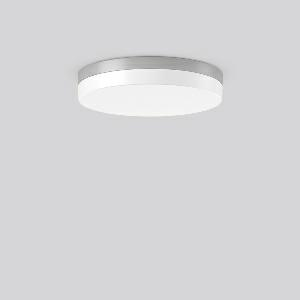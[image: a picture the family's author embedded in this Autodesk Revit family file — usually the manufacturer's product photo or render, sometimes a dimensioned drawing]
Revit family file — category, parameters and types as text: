
# Revit family: flat_slim_round_312632_004_c585
name_source: partatom
category: Lighting Fixtures
units: mm (PartAtom-declared; Revit-internal decimal feet)

## family parameters
Cut with Voids When Loaded = No
Host = Face
Light Source = No
Part Type = Normal
Room Calculation Point = No
Round Connector Dimension = Use Diameter
Shared = No

## types (1)
- MultiLumen 1 830 (1 x LED Modul 830, 2400 lm, 3000)
    Apparent Load = 20 VA
    CIE Flux Codes = 39 70 90 83 100
    Color Rendering = 80
    Color Temperature = 3000
    Default Elevation = 1800 mm
    Height = 70 mm
    Lamp = 1 x LED Modul 830
    Lamp Light Flux = 2400 lm
    Lamp count = 1
    Length = 400 mm
    Lifetime = 50000 h
    Luminous efficacy = 120 lm/W
    Manufacturer = RZB
    ModVariant = No
    Model = 312632.004
    Mounting Place = Ceiling
    Mounting Type = Surface mounted
    Number of Poles = 1
    OnlyDefault = Yes
    Power Factor = 1
    Product Name = FLAT SLIM round
    Product group = Surface mounted ceiling and wall luminaires
    ProductGroupID = 305
    Protection Class = Protection class I
    Protection Degree = Degree of protection
    RLX_Detail_Level = 1
    RLX_Emergency_Light_Flux = 0 lm
    RLX_Emergency_Type = 0
    RLX_Emergency_Type_DB = No
    RlxData = <blob elided: 20409 chars, md5=00515fce>
    Socket = socket
    Standby Power = 0 W
    System Light Flux = 2400 lm
    System Power = 20 W
    Type Comments = MultiLumen 1 830
    Type Image = 312631.004.jpg
    URL = http://relux.com
    VarID = multilumen_1_830
    Voltage = 0 V
    Weight = 0.00 kg
    Width = 0 mm  [stored 0 ft]

note: [stored X ft] marks values corroborated as IEEE doubles in the binary element streams (Revit-internal decimal feet)

## geometry (parser evidence)
native form markers: Blend x4, Sweep x14
no freeform markers — native parametric forms only
